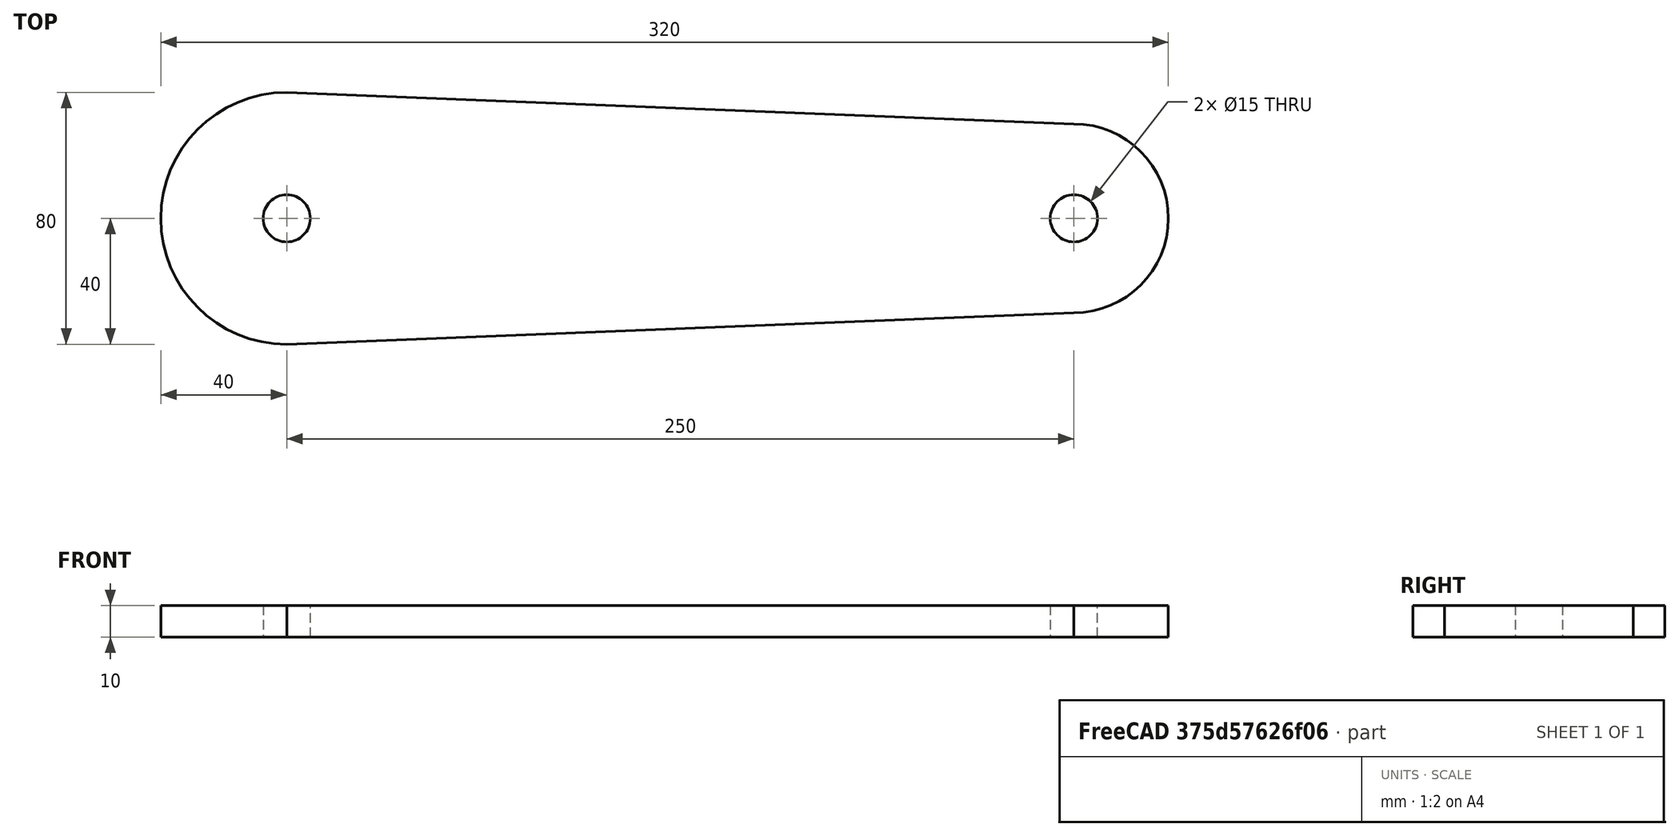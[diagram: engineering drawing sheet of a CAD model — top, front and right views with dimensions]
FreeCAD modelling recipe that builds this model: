
FCSTD DOCUMENT  (FreeCAD 0.18R4 (GitTag))
Label: upperArm
License: All rights reserved
LicenseURL: http://en.wikipedia.org/wiki/All_rights_reserved
objects: Drawing::FeatureViewPart×4, App::Part×1, Sketcher::SketchObject×1, PartDesign::Pad×1, PartDesign::Body×1, Drawing::FeaturePage×1, Part::Feature×1
note: 5 computed .brp shape members not serialized (recipe doc carries the construction recipe); baked Part::Feature solids carry a one-line shape summary decoded from their .brp

FEATURE [App::Part] Part
  Origin = -> Origin
FEATURE [Sketcher::SketchObject] Sketch
  MapMode = 5
  Support = -> [XY_Plane001]
  sketch-geometry (6):
    g0: ArcOfCircle CenterX=250 CenterY=0 CenterZ=0 NormalX=0 NormalY=0 NormalZ=1 AngleXU=0 Radius=30 StartAngle=4.71239 EndAngle=7.85398
    g1: LineSegment StartX=0 StartY=-40 StartZ=0 EndX=250 EndY=-30 EndZ=0
    g2: LineSegment StartX=0 StartY=40 StartZ=0 EndX=250 EndY=30 EndZ=0
    g3: Circle CenterX=0 CenterY=0 CenterZ=0 NormalX=0 NormalY=0 NormalZ=1 AngleXU=0 Radius=7.5
    g4: Circle CenterX=250 CenterY=0 CenterZ=0 NormalX=0 NormalY=0 NormalZ=1 AngleXU=0 Radius=7.5
    g5: ArcOfCircle CenterX=0 CenterY=0 CenterZ=0 NormalX=0 NormalY=0 NormalZ=1 AngleXU=0 Radius=40 StartAngle=1.5708 EndAngle=4.71239
  constraints (17):
    c: Vertical(g1,g0)
    c: Radius(g0) = 30
    c: Vertical(g2,g0)
    c: Diameter(g3) = 15
    c: Diameter(g4) = 15
    c: Coincident(g4,g0)
    c: Coincident(g0,g1)
    c: Coincident(g0,g2)
    c: Vertical(g1,g3)
    c: Vertical(g3,g2)
    c: Coincident(g5,g2)
    c: Coincident(g1,g5)
    c: Coincident(g5,g-1)
    c: Coincident(g3,g5)
    c: Radius(g5) = 40
    c: Horizontal(g3,g0)
    c: DistanceX(g3,g0) = 250
FEATURE [PartDesign::Pad] Pad
  Length = 10
  Length2 = 100
  Profile = -> Sketch
  Type = 0
FEATURE [PartDesign::Body] Body  label="Upper Arm"
  Group = -> [Sketch,Pad]
  Origin = -> Origin001
  Tip = -> Pad
FEATURE [Drawing::FeatureViewPart] Ortho  label="Ortho_0_0"
  Direction = (1,0,0)
  HiddenWidth = 0.15
  LineWidth = 0.35
  Rotation = -90
  Scale = 0.5
  ShowHiddenLines = true
  ShowSmoothLines = false
  Source = -> Body
  Tolerance = 0.05
  ViewResult = <blob: 4335 chars omitted>
  Visible = false
  X = 96.7108
  Y = 209.623
FEATURE [Drawing::FeatureViewPart] Ortho006  label="Ortho_1_1"
  Direction = (0.57735,0.57735,0.57735)
  HiddenWidth = 0.15
  LineWidth = 0.35
  Rotation = 120
  Scale = 0.5
  ShowHiddenLines = true
  ShowSmoothLines = false
  Source = -> Body
  Tolerance = 0.05
  ViewResult = <blob: 3273 chars omitted>
  Visible = false
  X = 305.783
  Y = 84.8568
FEATURE [Drawing::FeatureViewPart] Ortho007  label="Ortho_1_0"
  Direction = (0,1,0)
  HiddenWidth = 0.15
  LineWidth = 0.35
  Rotation = -90
  Scale = 0.5
  ShowHiddenLines = true
  ShowSmoothLines = false
  Source = -> Body
  Tolerance = 0.05
  ViewResult = <blob: 4552 chars omitted>
  Visible = false
  X = 323.358
  Y = 209.623
FEATURE [Drawing::FeatureViewPart] Ortho008  label="Ortho_0_1"
  Direction = (0,0,1)
  HiddenWidth = 0.15
  LineWidth = 0.35
  Rotation = 90
  Scale = 0.5
  ShowHiddenLines = true
  ShowSmoothLines = false
  Source = -> Body
  Tolerance = 0.05
  ViewResult = <g id="Ortho_0_1"\n   transform="rotate(90,96.7108,47.3091) translate(96.7108,47.3091) scale(0.5,0.5)"\n  >\n<g   fill="none"\n   stroke="rgb(0, 0, 0)"\n   stroke-dasharray="0.2,0.1)"\n   stroke-linecap="butt"\n   stroke-linejoin="miter"\n   stroke-width="0.300000"\n   transform="scale(1,-1)"\n  >\n<path d="M250 -30 A30 30 0 0 1 250 30" /><path id= "2" d=" M 0 40 L 250 30 " />\n<path d="M-1.53143e-14 40 A40 40 0 0 1 -7.34788e-15 -40" /><path id= "4" d=" M 0 -40 L 250 -30 " />\n<circle cx ="250" cy ="0" r ="7.5" /><circle cx ="0" cy ="0" r ="7.5" /></g>\n<g   fill="none"\n   stroke="rgb(0, 0, 0)"\n   stroke-linecap="butt"\n   stroke-linejoin="miter"\n   stroke-width="0.700000"\n   transform="scale(1,-1)"\n  >\n<path d="M250 -30 A30 30 0 0 1 250 30" /><path id= "2" d=" M 0 40 L 250 30 " />\n<path d="M-1.53143e-14 40 A40 40 0 0 1 -7.34788e-15 -40" /><path id= "4" d=" M 0 -40 L 250 -30 " />\n<circle cx ="250" cy ="0" r ="7.5" /><circle cx ="0" cy ="0" r ="7.5" /></g>\n</g>
  Visible = false
  X = 96.7108
  Y = 47.3091
FEATURE [Drawing::FeaturePage] Page
  EditableTexts = L. Cañamar Amaya | March 19, 2021 | A. A. Pech Che | 1:0.5 | 4 | 1 | Upper Arm | base to forearm
  Group = -> [Ortho,Ortho006,Ortho007,Ortho008]
  Template = D:/Installed Programs/FreeCAD 0.18/data/Mod/Drawing/Templates/A3_Landscape.svg
FEATURE [Part::Feature] Pad001  label="Robot_UpperArm"
  shape: bbox 320 x 80 x 10 mm, 8 faces (baked)
